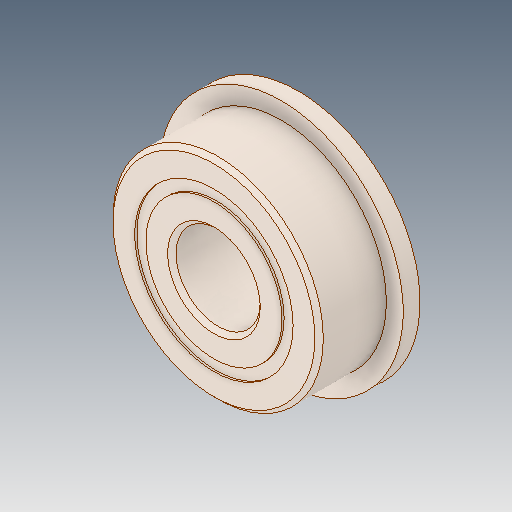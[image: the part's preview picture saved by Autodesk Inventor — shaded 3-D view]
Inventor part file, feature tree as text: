
AUTODESK INVENTOR PART (.ipt)
format: ipt  version: 2019 (Build 230136000, 136)  size: 630,272 bytes
history: native  units: mm
features: other x11, revolve x5
ambient origin geometry x8: Origin, YZ Plane, XZ Plane, XY Plane, X Axis, Y Axis, Z Axis, Center Point
bodies: Solid1 (feature_tree), Solid2 (feature_tree), Solid3 (feature_tree), Solid4 (feature_tree), Solid5 (feature_tree), Solid6 (feature_tree), Solid7 (feature_tree), Solid8 (feature_tree), Solid9 (feature_tree), Solid10 (feature_tree), Solid11 (feature_tree), Solid12 (feature_tree), Solid13 (feature_tree), Solid14 (feature_tree), Solid15 (feature_tree), Solid16 (feature_tree)
feature tree (16):
  revolve  "Revolve3"  [1 undecoded]
  revolve  "Revolve4"  [1 undecoded]
  other  "CirPattern1[1]"
  other  "CirPattern1[2]"
  other  "CirPattern1[3]"
  other  "CirPattern1[4]"
  other  "CirPattern1[5]"
  other  "CirPattern1[6]"
  other  "CirPattern1[7]"
  other  "CirPattern1[8]"
  other  "CirPattern1[9]"
  other  "CirPattern1[10]"
  other  "CirPattern1[11]"
  revolve  "Revolve5[1]"  [1 undecoded]
  revolve  "Revolve5[2]"  [1 undecoded]
  revolve  "Revolve6"  [1 undecoded]
note: 5 required parameter values undecoded (feature->parameter linkage not recoverable at this tier; creation-order binding heuristic only, values carry confidence <= 0.55)
